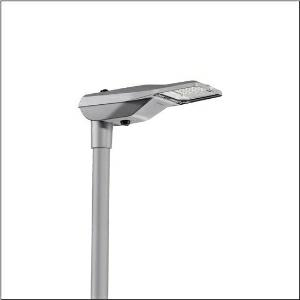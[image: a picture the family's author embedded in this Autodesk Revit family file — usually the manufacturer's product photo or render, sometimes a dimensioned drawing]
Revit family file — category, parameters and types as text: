
# Revit family: streetlight_sl_21_micro___stw1_0a_5xe1e43t08db_d620
name_source: partatom
category: Lighting Fixtures
units: mm (PartAtom-declared; Revit-internal decimal feet)

## family parameters
Cut with Voids When Loaded = No
Host = Face
Light Source = No
Part Type = Normal
Room Calculation Point = No
Round Connector Dimension = Use Diameter
Shared = No

## types (1)
- --- (1 x LED, 5320 lm, 39.1 W, 4000K)
    Apparent Load = 39 VA
    CIE Flux Codes = 38 75 98 100 100
    Color Rendering = 70
    Color Temperature = 4000K
    Default Elevation = 1800 mm
    Description = Streetlight SL 21 micro, mast luminaire, primary light control with lens, of PMMA, primary optical cover: cover, of toughened safety glass, transparent, light distribution: STW1.0a, light emission: direct distribution, primary light characteristic: asymmetric, installation type: side-entry, post-top, LED, High Power LED, rated luminous flux: 5.320lm, luminous efficacy: 136lm/W, light colour: 740, colour temperature: 4000K, control gear: D4i, control: flexible luminous flux parameterisation, time-dependent luminous flux control, constant luminous flux control, overheat protection, pre-setting: logarithmic dimming characteristic, mains connection: 220..240V, AC, 50/60Hz, start of lifetime: 39W, end of service life: 41W, reduction: 18W, luminaire housing, of diecast aluminium, powder-coated, SITECO metallic grey (DB 702S), corrosivity category C5 high according to DIN EN ISO 12944, please order mast flange separately, inclination adjustable: 0°, 5°, 10°, 15°, sealing non-destructively replaceable, multi-level sealing system, length: 528mm, width: 235mm, height: 110mm, mast flange for spigot size: 42mm (side-entry): 5XC10008XM4, 60/48mm (side-entry/post-top): 5XC10108XM2, 76/60mm (side-entry/post-top): 5XC10108XM1, Smart Interface below and above, protection rating (complete): IP66, insulation class (complete): insulation class II (safety insulation), certification: CE, ENEC, ENEC+, VDE, impact resistance: IK10, permissible operating ambient temperature for outdoor applications: -40..+50°C, standard-compliant lighting for roads and squares, packaging unit: 1 piece

Light Distribution: STW1.0a
    Height = 110 mm
    Lamp = 1 x LED
    Lamp Light Flux = 5320 lm
    Lamp Power = 39.1 W
    Lamp count = 1
    Length = 528 mm
    Luminous efficacy = 136 lm/W
    Manufacturer = Siteco
    ModVariant = No
    Model = 5XE1E43T08DB
    Number of Poles = 1
    OnlyDefault = Yes
    Power Factor = 1
    Product Name = Streetlight SL 21 micro | STW1.0a
    Product group = mast luminaire | pylon top
    ProductGroupID = 6100
    Protection Class = Protection class II
    Protection Degree = IP 66
    RLX_Detail_Level = 1
    RLX_Emergency_Light_Flux = 0 lm
    RLX_Emergency_Type = 0
    RLX_Emergency_Type_DB = No
    RlxData = <blob elided: 98945 chars, md5=df8df1db>
    Socket = socket
    Standby Power = 0 W
    System Light Flux = 5320 lm
    System Power = 39 W
    Type Comments = factory setting: luminous flux: 100 % | dim-lin: 254 | 765 mA
    Type Image = l_1007239.jpg
    URL = http://relux.com
    VarID = @adj_154725
    Voltage = 0 V
    Weight = 0.00 kg
    Width = 235 mm

## geometry (parser evidence)
native form markers: Blend x4, Sweep x10
no freeform markers — native parametric forms only
